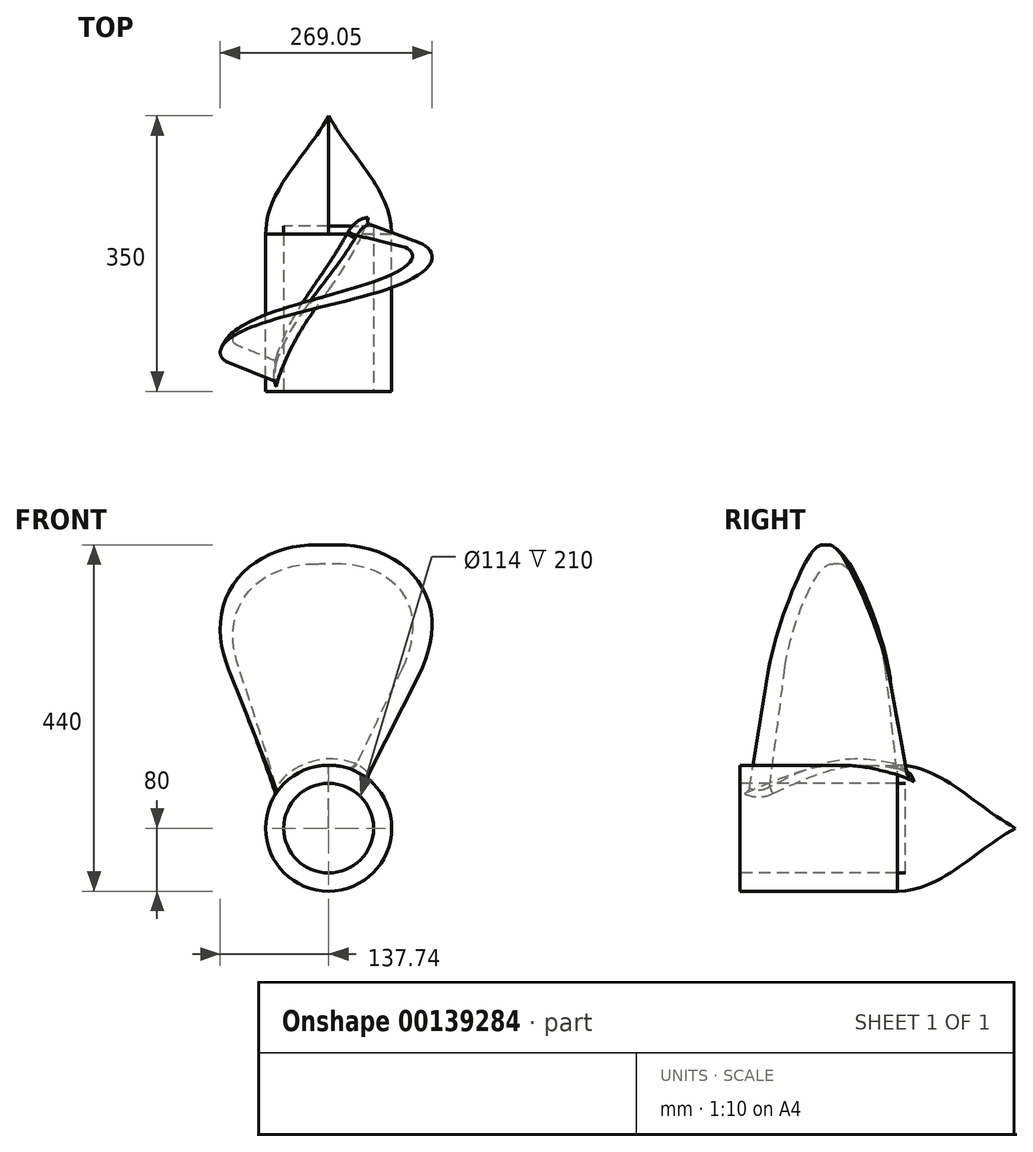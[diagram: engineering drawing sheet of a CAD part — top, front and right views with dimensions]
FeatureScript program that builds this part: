
annotation { "Feature Type Name" : "Feature", "Feature Type Description" : "" }
export const myFeature = defineFeature(function(context is Context, id is Id, definition is map)
    precondition{}
    {
        {
            var Q0;
            Q0=qCreatedBy(makeId("Right.planeOp"),FACE);
            var sketch = newSketch(context, id + "F0", { "sketchPlane" : qUnion([Q0])});
            skLineSegment(sketch, "E0", {"start": v(0, 0) * mm, "end": v(-350, 0) * mm});
            skLineSegment(sketch, "E1", {"start": v(-350, 0) * mm, "end": v(-350, 80) * mm});
            skLineSegment(sketch, "E2", {"start": v(-350, 80) * mm, "end": v(-150, 80) * mm});
            skFitSpline(sketch, "E3", {"points": [v(0, 0) * mm, v(-150, 80) * mm], "startDerivative": vector(-150, 80) * mm, "endDerivative": vector(-170, 0) * mm});
            skSolve(sketch);
        }
        {
            var Q0;
            Q0=makeQuery(id+"F0.imprint","IMPRINT",FACE,{"disambiguationData":[TD([[makeQuery(id+"F0.imprint","IMPRINT",EDGE,{"derivedFrom":sQuery(id+"F0.wireOp",EDGE,"E0")}),-1.0]])]});
            var Q1;
            Q1=sQuery(id+"F0.wireOp",EDGE,"E0");
            revolve(context, id + "F1", {"entities" : qUnion([Q0]), "axis" : qUnion([Q1]), "revolveType" : RevolveType.FULL});
        }
        {
            var Q0;
            Q0=qCreatedBy(makeId("Top.planeOp"),FACE);
            var sketch = newSketch(context, id + "F2", { "sketchPlane" : qUnion([Q0])});
            skLineSegment(sketch, "E4.bottom", {"start": v(-58.54, -342.78) * mm, "end": v(-47, -346.1) * mm});
            skLineSegment(sketch, "E4.top", {"start": v(4.86, -121.7) * mm, "end": v(16.4, -125) * mm});
            skLineSegment(sketch, "E4.left", {"start": v(-58.54, -342.78) * mm, "end": v(4.86, -121.7) * mm});
            skLineSegment(sketch, "E4.right", {"start": v(-47, -346.1) * mm, "end": v(16.4, -125) * mm});
            skLineSegment(sketch, "E5", {"start": v(0, 0) * mm, "end": v(0, -513.39) * mm, "construction": true});
            skSolve(sketch);
        }
        {
            var Q0;
            Q0=qCreatedBy(makeId("Top.planeOp"),FACE);
            cPlane(context, id + "F3", {"entities" : qUnion([Q0]), "cplaneType" : CPlaneType.OFFSET, "offset" : 360 * mm, "width" : 150 * mm, "height" : 150 * mm});
        }
        {
            var Q0;
            Q0=qCreatedBy(id+"F3.planeOp",FACE);
            var sketch = newSketch(context, id + "F4", { "sketchPlane" : qUnion([Q0])});
            skLineSegment(sketch, "E6.bottom", {"start": v(-190, -288) * mm, "end": v(-192.9, -276.36) * mm});
            skLineSegment(sketch, "E6.top", {"start": v(198.12, -191.23) * mm, "end": v(195.22, -179.59) * mm});
            skLineSegment(sketch, "E6.left", {"start": v(-190, -288) * mm, "end": v(198.12, -191.23) * mm});
            skLineSegment(sketch, "E6.right", {"start": v(-192.9, -276.36) * mm, "end": v(195.22, -179.59) * mm});
            skSolve(sketch);
        }
        {
            var Q1;
            Q1 = qSketchRegion(id + "F2", true);
            var Q2;
            Q2 = qSketchRegion(id + "F4", true);
            loft(context, id + "F5", {"operationType" : NewBodyOperationType.ADD, "sheetProfilesArray" : [{ "sheetProfileEntities" : qUnion([Q1]) }, { "sheetProfileEntities" : qUnion([Q2]) }]});
        }
        {
            var Q0;
            Q0=makeQuery(id+"F5.opLoft","MID_CAP_EDGE",EDGE,{"disambiguationData":[OSD([sQuery(id+"F4.wireOp",EDGE,"E6.top"),sQuery(id+"F4.wireOp",EDGE,"E6.left"),sQuery(id+"F4.wireOp",EDGE,"E6.right")])],"capPos":1.0});
            var Q1;
            Q1=makeQuery(id+"F5.opLoft","MID_CAP_EDGE",EDGE,{"disambiguationData":[OSD([sQuery(id+"F4.wireOp",EDGE,"E6.bottom"),sQuery(id+"F4.wireOp",EDGE,"E6.left"),sQuery(id+"F4.wireOp",EDGE,"E6.right")])],"capPos":1.0});
            fillet(context, id + "F6", {"entities" : qUnion([Q0, Q1]), "radius" : 132.5 * mm, "tangentPropagation" : true, "allowEdgeOverflow" : false});
        }
        {
            var Q0;
            Q0=makeQuery(id+"F5.opLoft","SWEPT_EDGE",EDGE,{"disambiguationData":[OSD([sQuery(id+"F2.wireOp",EDGE,"E4.top"),sQuery(id+"F2.wireOp",EDGE,"E4.left"),sQuery(id+"F4.wireOp",EDGE,"E6.top"),sQuery(id+"F4.wireOp",EDGE,"E6.right")])]});
            fillet(context, id + "F7", {"entities" : qUnion([Q0]), "radius" : 30 * mm, "tangentPropagation" : true, "allowEdgeOverflow" : false});
        }
        {
            var Q0;
            Q0=makeQuery(id+"F5.boolean.opBoolean","INTERSECT",EDGE,{"derivedFrom":[makeQuery(id+"F1.opRevolve","SWEPT_FACE",FACE,{"disambiguationData":[OSD([sQuery(id+"F0.wireOp",EDGE,"E2")])]}),makeQuery(id+"F5.opLoft","SWEPT_FACE",FACE,{"disambiguationData":[OSD([sQuery(id+"F2.wireOp",EDGE,"E4.bottom"),sQuery(id+"F2.wireOp",EDGE,"E4.top"),sQuery(id+"F2.wireOp",EDGE,"E4.left"),sQuery(id+"F4.wireOp",EDGE,"E6.bottom"),sQuery(id+"F4.wireOp",EDGE,"E6.top"),sQuery(id+"F4.wireOp",EDGE,"E6.right")])]})]});
            fillet(context, id + "F8", {"entities" : qUnion([Q0]), "radius" : 10 * mm, "tangentPropagation" : true, "allowEdgeOverflow" : false});
        }
        {
            var Q0;
            Q0=makeQuery(id+"F1.opRevolve","SWEPT_FACE",FACE,{"disambiguationData":[OSD([sQuery(id+"F0.wireOp",EDGE,"E1")])]});
            var sketch = newSketch(context, id + "F9", { "sketchPlane" : qUnion([Q0])});
            skCircle(sketch, "E7", {"center": v(0, 0) * mm, "radius": 57 * mm});
            skSolve(sketch);
        }
        {
            var Q0;
            Q0=makeQuery(id+"F9.imprint","IMPRINT",FACE,{"disambiguationData":[TD([[makeQuery(id+"F9.imprint","IMPRINT",EDGE,{"derivedFrom":sQuery(id+"F9.wireOp",EDGE,"E7")}),1.0]])]});
            extrude(context, id + "F10", {"entities" : qUnion([Q0]), "operationType" : NewBodyOperationType.REMOVE, "oppositeDirection" : true, "depth" : 210 * mm});
        }
    });
